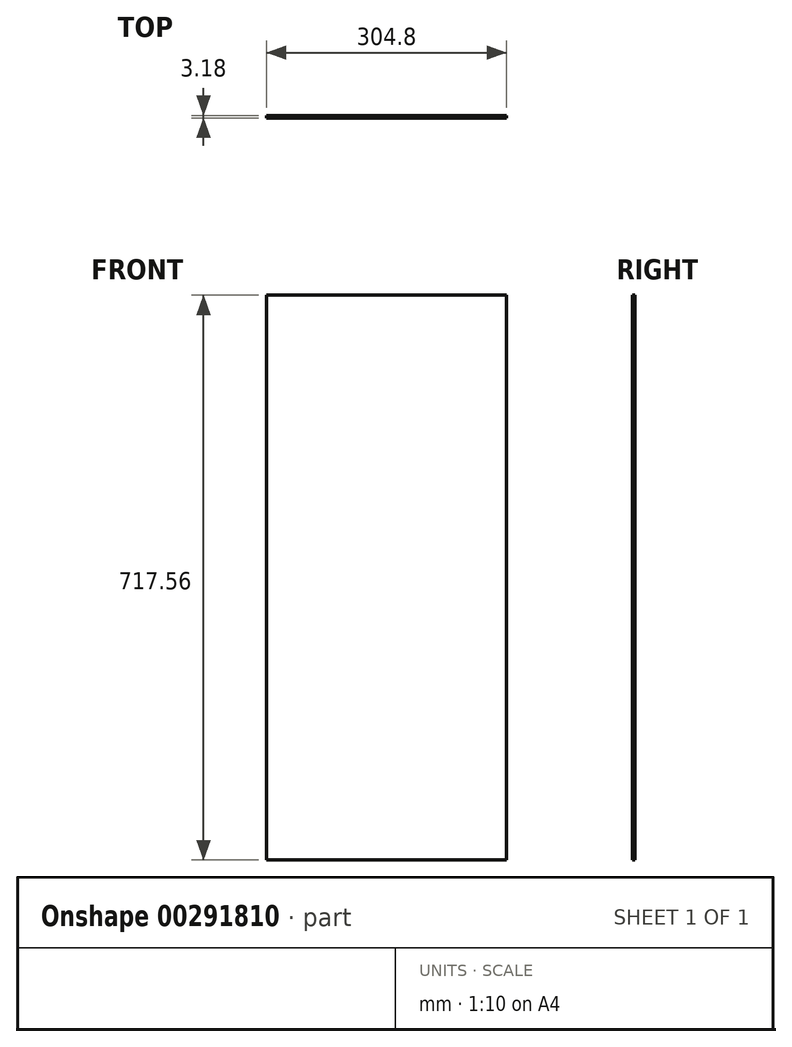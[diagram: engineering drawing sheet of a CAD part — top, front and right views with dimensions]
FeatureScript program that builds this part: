
annotation { "Feature Type Name" : "Feature", "Feature Type Description" : "" }
export const myFeature = defineFeature(function(context is Context, id is Id, definition is map)
    precondition{}
    {
        {
            var Q0;
            Q0=qCreatedBy(makeId("Front.planeOp"),FACE);
            var sketch = newSketch(context, id + "F0", { "sketchPlane" : qUnion([Q0])});
            skLineSegment(sketch, "E0.bottom", {"start": v(152.4, 358.78) * mm, "end": v(-152.4, 358.78) * mm});
            skLineSegment(sketch, "E0.top", {"start": v(152.4, -358.78) * mm, "end": v(-152.4, -358.78) * mm});
            skLineSegment(sketch, "E0.left", {"start": v(152.4, 358.78) * mm, "end": v(152.4, -358.78) * mm});
            skLineSegment(sketch, "E0.right", {"start": v(-152.4, 358.78) * mm, "end": v(-152.4, -358.78) * mm});
            skPoint(sketch, "E0.middle", {"position": v(0, 0) * mm});
            skSolve(sketch);
        }
        {
            var Q0;
            Q0 = qSketchRegion(id + "F0", true);
            extrude(context, id + "F1", {"entities" : qUnion([Q0]), "endBound" : BoundingType.SYMMETRIC, "depth" : 3.17 * mm});
        }
    });
